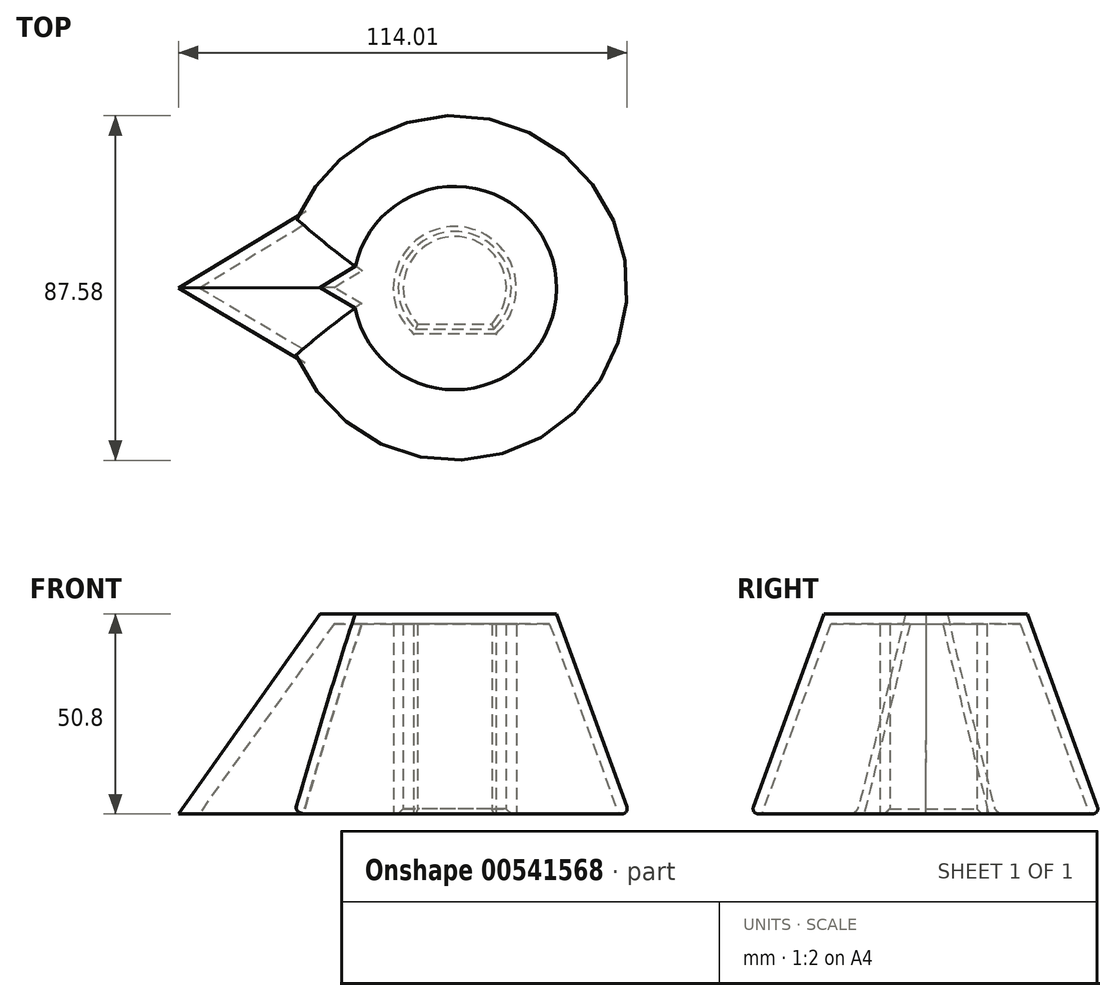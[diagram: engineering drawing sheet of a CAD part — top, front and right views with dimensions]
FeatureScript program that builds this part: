
annotation { "Feature Type Name" : "Feature", "Feature Type Description" : "" }
export const myFeature = defineFeature(function(context is Context, id is Id, definition is map)
    precondition{}
    {
        {
            var Q0;
            Q0=qCreatedBy(makeId("Top.planeOp"),FACE);
            var sketch = newSketch(context, id + "F0", { "sketchPlane" : qUnion([Q0])});
            skArc(sketch, "E0", {"start": v(-40.76, -17.44) * mm, "mid": v(44.33, -0.24) * mm, "end": v(-40.56, 17.89) * mm});
            skLineSegment(sketch, "E1", {"start": v(-40.56, 17.89) * mm, "end": v(-70.22, 0) * mm});
            skLineSegment(sketch, "E2", {"start": v(-70.22, 0) * mm, "end": v(-40.76, -17.44) * mm});
            skSolve(sketch);
        }
        {
            var Q0;
            Q0 = qSketchRegion(id + "F0", true);
            extrude(context, id + "F1", {"entities" : qUnion([Q0]), "depth" : 50.8 * mm, "offsetDistance" : 25.4 * mm, "hasDraft" : true, "draftAngle" : 20 * degree, "draftPullDirection" : true});
        }
        {
            var Q0;
            Q0=makeQuery(id+"F1.opExtrude","CAP_FACE",FACE,{"disambiguationData":[OSD([sQuery(id+"F0.wireOp",EDGE,"E0"),sQuery(id+"F0.wireOp",EDGE,"E1"),sQuery(id+"F0.wireOp",EDGE,"E2")])],"isStart":true});
            var sketch = newSketch(context, id + "F2", { "sketchPlane" : qUnion([Q0])});
            skArc(sketch, "E3", {"start": v(-9.41, 9.09) * mm, "mid": v(0, -13.08) * mm, "end": v(9.41, 9.09) * mm});
            skLineSegment(sketch, "E4", {"start": v(-9.41, 9.09) * mm, "end": v(9.41, 9.09) * mm});
            skSolve(sketch);
        }
        {
            var Q0;
            Q0 = qSketchRegion(id + "F2", true);
            extrude(context, id + "F3", {"entities" : qUnion([Q0]), "operationType" : NewBodyOperationType.REMOVE, "oppositeDirection" : true, "depth" : 170.18 * mm, "offsetDistance" : 25.4 * mm});
        }
        {
            var Q0;
            Q0=makeQuery(id+"F1.opExtrude","CAP_FACE",FACE,{"disambiguationData":[OSD([sQuery(id+"F0.wireOp",EDGE,"E0"),sQuery(id+"F0.wireOp",EDGE,"E1"),sQuery(id+"F0.wireOp",EDGE,"E2")])],"isStart":true});
            shell(context, id + "F4", {"entities" : qUnion([Q0]), "thickness" : 2.54 * mm});
        }
        {
            var Q0;
            Q0=makeQuery(id+"F4.opShell","OFFSET_EDGE",EDGE,{"disambiguationData":[OSD([sQuery(id+"F0.wireOp",EDGE,"E0"),sQuery(id+"F2.wireOp",EDGE,"E3")])]});
            var Q1;
            Q1=makeQuery(id+"F4.opShell","OFFSET_EDGE",EDGE,{"disambiguationData":[OSD([sQuery(id+"F0.wireOp",EDGE,"E0"),sQuery(id+"F2.wireOp",EDGE,"E4")])]});
            fillet(context, id + "F5", {"entities" : qUnion([Q0, Q1]), "radius" : 0.25 * mm, "tangentPropagation" : true, "allowEdgeOverflow" : false});
        }
        {
            var Q0;
            Q0=makeQuery(id+"F1.opExtrude","CAP_EDGE",EDGE,{"disambiguationData":[OSD([sQuery(id+"F0.wireOp",EDGE,"E0")])],"isStart":true});
            fillet(context, id + "F6", {"entities" : qUnion([Q0]), "radius" : 1.27 * mm, "tangentPropagation" : true, "allowEdgeOverflow" : false});
        }
        {
            var Q0;
            Q0=makeQuery(id+"F3.boolean.opBoolean","INTERSECT",EDGE,{"derivedFrom":[makeQuery(id+"F1.opExtrude","CAP_FACE",FACE,{"disambiguationData":[OSD([sQuery(id+"F0.wireOp",EDGE,"E0"),sQuery(id+"F0.wireOp",EDGE,"E1"),sQuery(id+"F0.wireOp",EDGE,"E2")])],"isStart":true}),makeQuery(id+"F3.opExtrude","SWEPT_FACE",FACE,{"disambiguationData":[OSD([sQuery(id+"F2.wireOp",EDGE,"E4")])]})]});
            var Q1;
            Q1=makeQuery(id+"F3.boolean.opBoolean","INTERSECT",EDGE,{"derivedFrom":[makeQuery(id+"F1.opExtrude","CAP_FACE",FACE,{"disambiguationData":[OSD([sQuery(id+"F0.wireOp",EDGE,"E0"),sQuery(id+"F0.wireOp",EDGE,"E1"),sQuery(id+"F0.wireOp",EDGE,"E2")])],"isStart":true}),makeQuery(id+"F3.opExtrude","SWEPT_FACE",FACE,{"disambiguationData":[OSD([sQuery(id+"F2.wireOp",EDGE,"E3")])]})]});
            chamfer(context, id + "F7", {"entities" : qUnion([Q0, Q1]), "width" : 1.27 * mm, "tangentPropagation" : true});
        }
        {
            var Q0;
            Q0=makeQuery(id+"F1.opExtrude","CAP_FACE",FACE,{"disambiguationData":[OSD([sQuery(id+"F0.wireOp",EDGE,"E0"),sQuery(id+"F0.wireOp",EDGE,"E1"),sQuery(id+"F0.wireOp",EDGE,"E2")])],"isStart":false});
            var sketch = newSketch(context, id + "F8", { "sketchPlane" : qUnion([Q0])});
            skCircle(sketch, "E5", {"center": v(0, 2.97) * mm, "radius": 21.57 * mm});
            skSolve(sketch);
        }
        {
            var Q0;
            Q0 = qSketchRegion(id + "F8", true);
            extrude(context, id + "F9", {"entities" : qUnion([Q0]), "operationType" : NewBodyOperationType.ADD, "oppositeDirection" : true, "depth" : 2.54 * mm, "offsetDistance" : 25.4 * mm});
        }
    });
